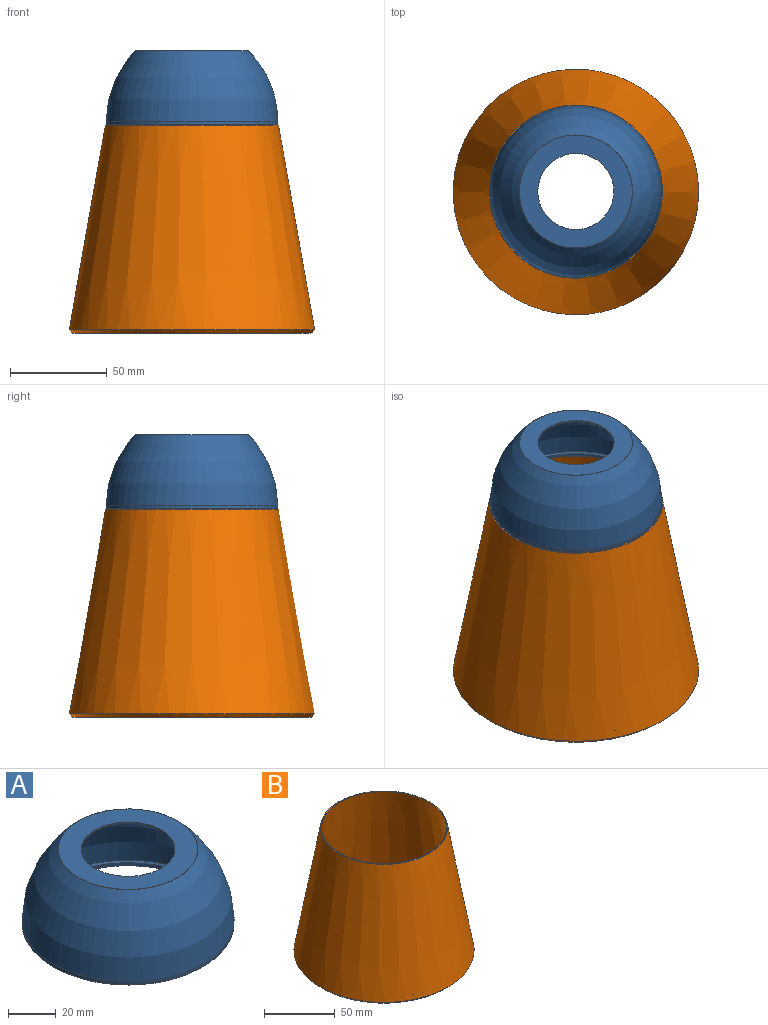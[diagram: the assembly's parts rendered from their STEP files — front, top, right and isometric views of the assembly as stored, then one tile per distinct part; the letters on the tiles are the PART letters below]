
ASSEMBLY  parts=2 mates=1
PART A: 13 faces, bbox 88.9x88.9x38.9 mm
  f0: cylinder r=44.45mm len=88.9mm, axis (0,0,-1), area 390.2mm2, adj f2,f4
  f1: plane 58.42x58.42mm, normal (0,0,1), area 1463.1mm2, adj f3,f12
  f2: plane 88.9x88.9mm, normal (0,0,-1), area 211mm2, adj f0,f5
  f3: cone r=29.21mm half-angle=45deg, axis (0,0,-1), area 16.5mm2, adj f1,f4
  f4: revolved ~88.9x88.9mm, area 10045.2mm2, adj f0,f3
  f5: cylinder r=43.69mm len=87.38mm, axis (0,0,-1), area 209.2mm2, adj f2,f7
  f6: cylinder r=42.93mm len=85.85mm, axis (0,0,-1), area 411mm2, adj f7,f11
  f7: plane 87.38x87.38mm, normal (0,0,-1), area 207.3mm2, adj f5,f6
  f8: plane 56.9x56.9mm, normal (0,0,-1), area 1325.1mm2, adj f9,f12
  f9: cone r=43.69mm half-angle=45deg, axis (0,0,-1), area 16.1mm2, adj f8,f10
  f10: revolved ~87.36x87.36mm, area 9606.4mm2, adj f9,f11
  f11: cone r=42.93mm half-angle=45deg, axis (0,0,1), area 292.5mm2, adj f6,f10
  f12: cylinder r=19.69mm len=39.37mm, axis (0,0,1), area 94.2mm2, adj f1,f8
PART B: 12 faces, bbox 134.5x134.5x107.8 mm
  f0: cone r=63.5mm half-angle=10deg, axis (0,0,-1), area 36600.9mm2, adj f10,f11
  f1: torus R=19.79mm, axis (0,0,1), area 11.1mm2, adj f5,f11
  f2: cylinder r=57.79mm len=115.57mm, axis (0,0,-1), area 691.7mm2, adj f3,f4
  f3: plane 123.19x123.19mm, normal (0,0,-1), area 1428.9mm2, adj f2,f10
  f4: plane 117.09x117.09mm, normal (0,0,1), area 278.5mm2, adj f2,f6
  f5: cone r=62.75mm half-angle=10deg, axis (0,0,-1), area 34607.2mm2, adj f1,f9
  f6: cylinder r=58.55mm len=117.09mm, axis (0,0,-1), area 420.5mm2, adj f4,f8
  f7: cylinder r=60.2mm len=120.4mm, axis (0,0,-1), area 720.5mm2, adj f8,f9
  f8: plane 120.4x120.4mm, normal (0,0,1), area 615.9mm2, adj f6,f7
  f9: torus R=59.58mm, axis (0,0,-1), area 1471.5mm2, adj f5,f7
  f10: cone r=60.96mm half-angle=45deg, axis (0,0,1), area 1058.8mm2, adj f0,f3
  f11: plane 89.65x89.65mm, normal (0,0,1), area 216mm2, adj f0,f1
PLACE A t=(43.29,-14.92,52.28)mm
PLACE B t=(16.76,9.31,-54.03)mm
MATE cylindrical A.f0 <-> B.f0  axis (0,0,-1) through (16.76,9.31,52.28)mm
